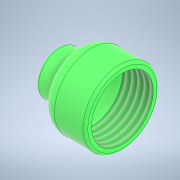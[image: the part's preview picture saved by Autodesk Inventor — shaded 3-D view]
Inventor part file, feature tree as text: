
AUTODESK INVENTOR PART (.ipt)
format: ipt  version: 2021 (Build 250183000, 183)  size: 228,864 bytes
history: native  units: mm
features: fillet x2, thicken_offset x1, thread x1, sketch x1, other x1, revolve x1
ambient origin geometry x8: Origin, YZ Plane, XZ Plane, XY Plane, X Axis, Y Axis, Z Axis, Center Point
bodies: Solid1 (feature_tree)
feature tree (7):
  thicken_offset  "Thicken1"
  thread  "Thread1"  [1 undecoded]
  fillet  "Fillet1"  Radius=6.0mm
  fillet  "Fillet2"  Radius=1.5mm
  sketch  "Sketch1"  dims[d3=1.25mm d4=2.5mm d5=3.5mm d6=5.25mm d7=0.0mm d8=4.270655mm d9=3.148074mm d10=5.940384mm d11=90.0deg d12=0.5mm d13=0.5mm d14=160.0mm d15=0.0mm d16=0.2mm d17=0.2mm]
  other  "Srf1"
  revolve  "RevolutionSrf1"  [1 undecoded]
note: 2 required parameter values undecoded (feature->parameter linkage not recoverable at this tier; creation-order binding heuristic only, values carry confidence <= 0.55)